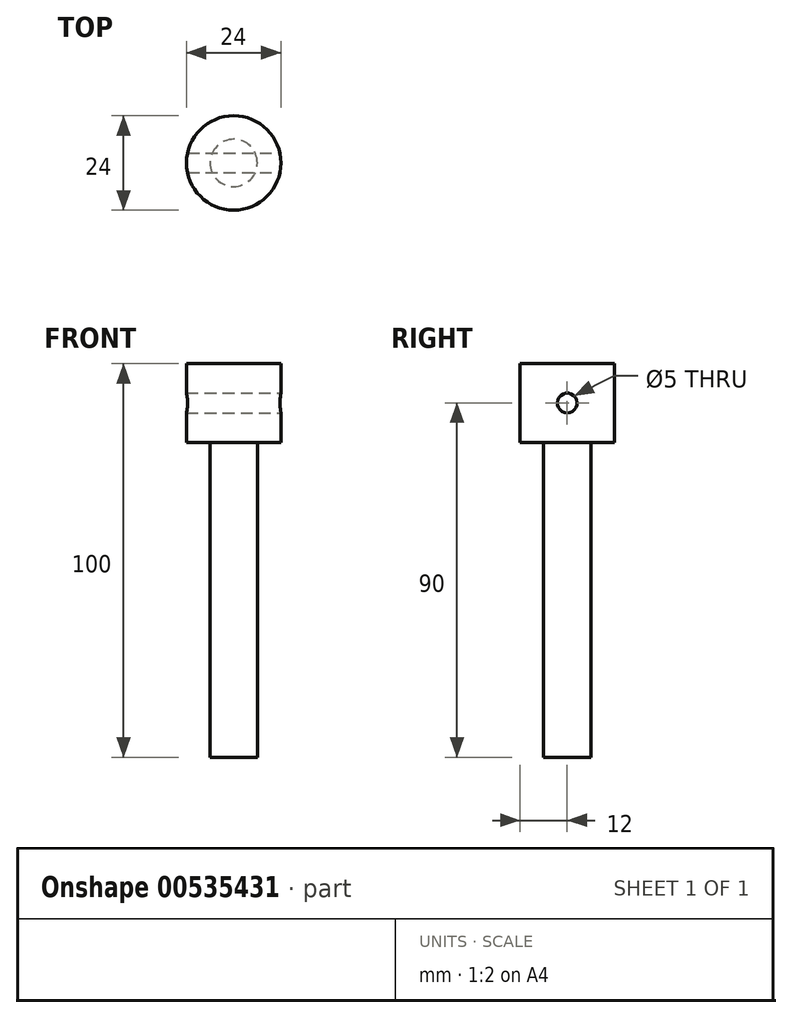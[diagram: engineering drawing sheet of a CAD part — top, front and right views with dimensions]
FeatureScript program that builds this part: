
annotation { "Feature Type Name" : "Feature", "Feature Type Description" : "" }
export const myFeature = defineFeature(function(context is Context, id is Id, definition is map)
    precondition{}
    {
        {
            var Q0;
            Q0=qCreatedBy(makeId("Front.planeOp"),FACE);
            var sketch = newSketch(context, id + "F0", { "sketchPlane" : qUnion([Q0])});
            skLineSegment(sketch, "E0", {"start": v(0, 0) * mm, "end": v(0, 100) * mm});
            skLineSegment(sketch, "E1.0", {"start": v(6, 0) * mm, "end": v(6, 80) * mm});
            skLineSegment(sketch, "E2", {"start": v(0, 0) * mm, "end": v(6, 0) * mm});
            skLineSegment(sketch, "E3", {"start": v(0, 100) * mm, "end": v(12, 100) * mm});
            skLineSegment(sketch, "E4", {"start": v(12, 100) * mm, "end": v(12, 80) * mm});
            skLineSegment(sketch, "E5", {"start": v(12, 80) * mm, "end": v(6, 80) * mm});
            skSolve(sketch);
        }
        {
            var Q0;
            Q0 = qSketchRegion(id + "F0", true);
            var Q1;
            Q1=sQuery(id+"F0.wireOp",EDGE,"E0");
            revolve(context, id + "F1", {"entities" : qUnion([Q0]), "axis" : qUnion([Q1]), "revolveType" : RevolveType.FULL});
        }
        {
            var Q0;
            Q0=qCreatedBy(makeId("Right.planeOp"),FACE);
            var sketch = newSketch(context, id + "F2", { "sketchPlane" : qUnion([Q0])});
            skLineSegment(sketch, "E6", {"start": v(0, 100) * mm, "end": v(-9.91, 100) * mm, "construction": true});
            skLineSegment(sketch, "E7", {"start": v(0, 100) * mm, "end": v(0, 80) * mm, "construction": true});
            skCircle(sketch, "E8", {"center": v(0, 90) * mm, "radius": 2.5 * mm});
            skSolve(sketch);
        }
        {
            var Q0;
            Q0 = qSketchRegion(id + "F2", true);
            extrude(context, id + "F3", {"entities" : qUnion([Q0]), "operationType" : NewBodyOperationType.REMOVE, "endBound" : BoundingType.SYMMETRIC, "oppositeDirection" : true, "depth" : 25 * mm, "offsetDistance" : 25 * mm});
        }
    });
